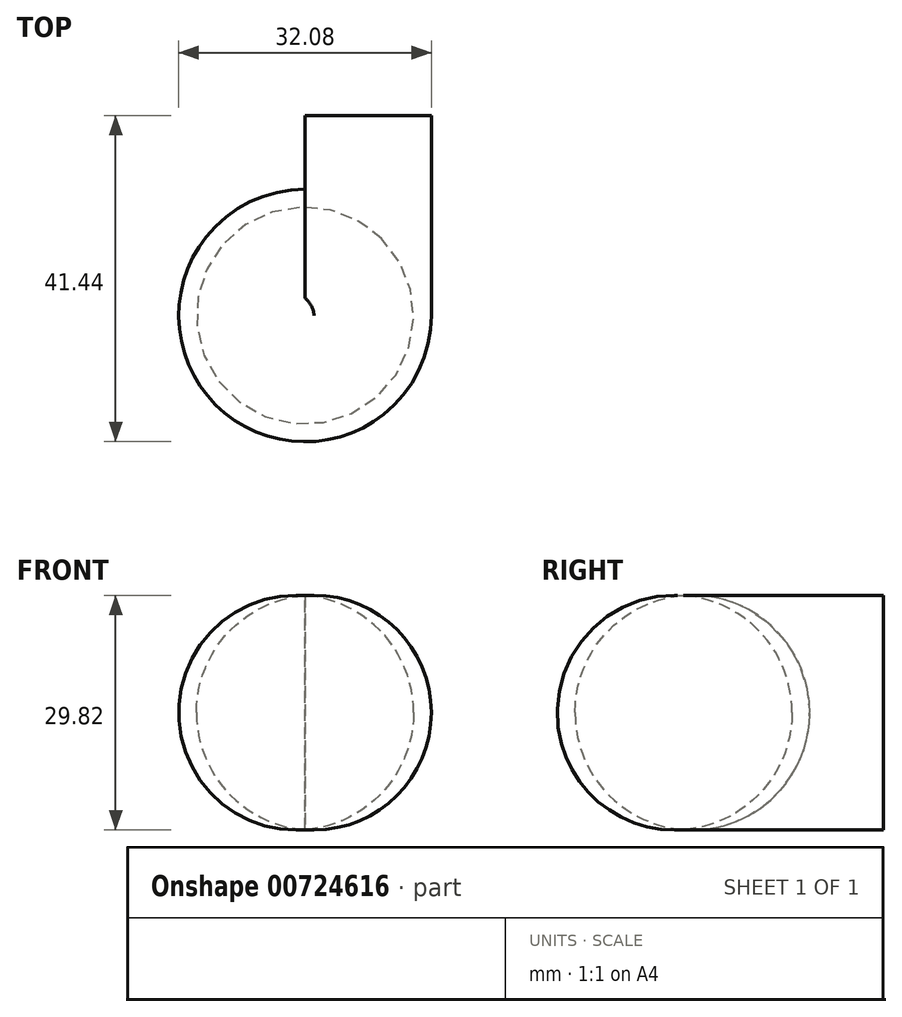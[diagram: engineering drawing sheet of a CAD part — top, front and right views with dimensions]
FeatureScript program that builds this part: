
annotation { "Feature Type Name" : "Feature", "Feature Type Description" : "" }
export const myFeature = defineFeature(function(context is Context, id is Id, definition is map)
    precondition{}
    {
        {
            var Q0;
            Q0=qCreatedBy(makeId("Front.planeOp"),FACE);
            var sketch = newSketch(context, id + "F0", { "sketchPlane" : qUnion([Q0])});
            skLineSegment(sketch, "E0", {"start": v(0, 16.42) * mm, "end": v(0, -13.32) * mm});
            skArc(sketch, "E1", {"start": v(0, -13.32) * mm, "mid": v(16.04, 1.55) * mm, "end": v(0, 16.42) * mm});
            skSolve(sketch);
        }
        {
            var Q0;
            Q0 = qSketchRegion(id + "F0", true);
            extrude(context, id + "F1", {"entities" : qUnion([Q0]), "depth" : 25.4 * mm, "offsetDistance" : 25.4 * mm});
        }
        {
            var Q0;
            Q0=makeQuery(id+"F1.opExtrude","CAP_FACE",FACE,{"disambiguationData":[OSD([sQuery(id+"F0.wireOp",EDGE,"E0"),sQuery(id+"F0.wireOp",EDGE,"E1")])],"isStart":false});
            var Q1;
            Q1=makeQuery(id+"F1.opExtrude","CAP_EDGE",EDGE,{"disambiguationData":[OSD([sQuery(id+"F0.wireOp",EDGE,"E0")])],"isStart":false});
            revolve(context, id + "F2", {"operationType" : NewBodyOperationType.ADD, "surfaceOperationType" : NewSurfaceOperationType.NEW, "entities" : qUnion([Q0]), "axis" : qUnion([Q1]), "revolveType" : RevolveType.FULL});
        }
    });
